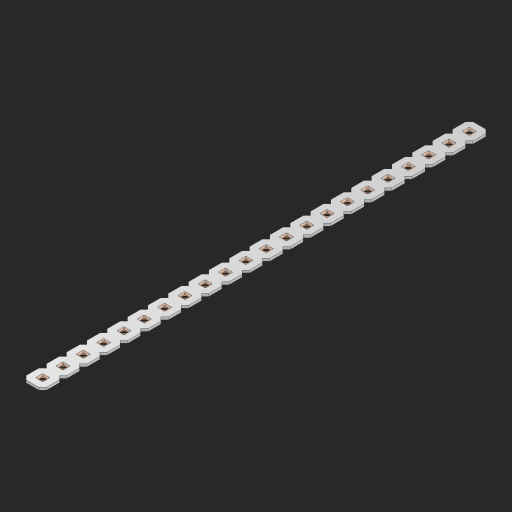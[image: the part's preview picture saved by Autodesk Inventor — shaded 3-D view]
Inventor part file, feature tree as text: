
AUTODESK INVENTOR PART (.ipt)
format: ipt  version: 2023 (Build 270158000, 158)  size: 514,560 bytes
history: native  units: in
note: dims shown in document units (in); Inventor stores cm internally (conversion verified against a paired STEP export)
features: other x23, extrude x21, sketch x2, pattern_linear x1
ambient origin geometry x8: Origin, YZ Plane, XZ Plane, XY Plane, X Axis, Y Axis, Z Axis, Center Point
bodies: Solid1 (feature_tree), Body (feature_tree)
feature tree (47):
  pattern_linear  "Rectangular Pattern1"  Spacing1=0.09in  [1 undecoded]
  sketch  "Sketch1"  dims[d1=0.5in]
  sketch  "Sketch2"  dims[d2=0.182in d3=0.09in d4=0.09in d5=0.09in d6=0.09in d7=0.09in d8=0.09in d9=0.09in d10=0.09in d11=0.02in d13=0.0in d14=0.172in d15=0.0625in d16=0.0in d19=0.5in d22=0.5in]
  other  "Srf1"
  other  "Srf126"
  other  "Srf127"
  other  "Srf128"
  other  "Srf129"
  other  "Srf130"
  other  "Srf131"
  other  "Srf250"
  other  "Srf251"
  other  "Srf252"
  other  "Srf253"
  other  "Srf254"
  other  "Srf255"
  other  "Srf256"
  other  "Srf257"
  other  "Srf258"
  other  "Srf259"
  other  "Srf260"
  other  "Srf261"
  other  "Srf262"
  other  "Srf263"
  other  "Srf264"
  other  "Circle"
  extrude  "ExtrusionSrf126"  Depth=0.09in
  extrude  "ExtrusionSrf127"  Depth=0.09in
  extrude  "ExtrusionSrf128"  Depth=0.09in
  extrude  "ExtrusionSrf129"  Depth=0.09in
  extrude  "ExtrusionSrf130"  Depth=0.09in
  extrude  "ExtrusionSrf131"  Depth=0.09in
  extrude  "ExtrusionSrf250"  Depth=0.09in
  extrude  "ExtrusionSrf251"  Depth=0.02in
  extrude  "ExtrusionSrf252"  TaperAngle=0.0deg  [1 undecoded]
  extrude  "ExtrusionSrf253"  Depth=0.5in
  extrude  "ExtrusionSrf254"  Depth=0.0625in TaperAngle=0.0deg
  extrude  "ExtrusionSrf255"  Depth=0.5in
  extrude  "ExtrusionSrf256"  Depth=0.5in
  extrude  "ExtrusionSrf257"  [1 undecoded]
  extrude  "ExtrusionSrf258"  [1 undecoded]
  extrude  "ExtrusionSrf259"  [1 undecoded]
  extrude  "ExtrusionSrf260"  [1 undecoded]
  extrude  "ExtrusionSrf261"  [1 undecoded]
  extrude  "ExtrusionSrf262"  [1 undecoded]
  extrude  "ExtrusionSrf263"  [1 undecoded]
  extrude  "ExtrusionSrf264"  [1 undecoded]
note: 10 required parameter values undecoded (feature->parameter linkage not recoverable at this tier; creation-order binding heuristic only, values carry confidence <= 0.55)
